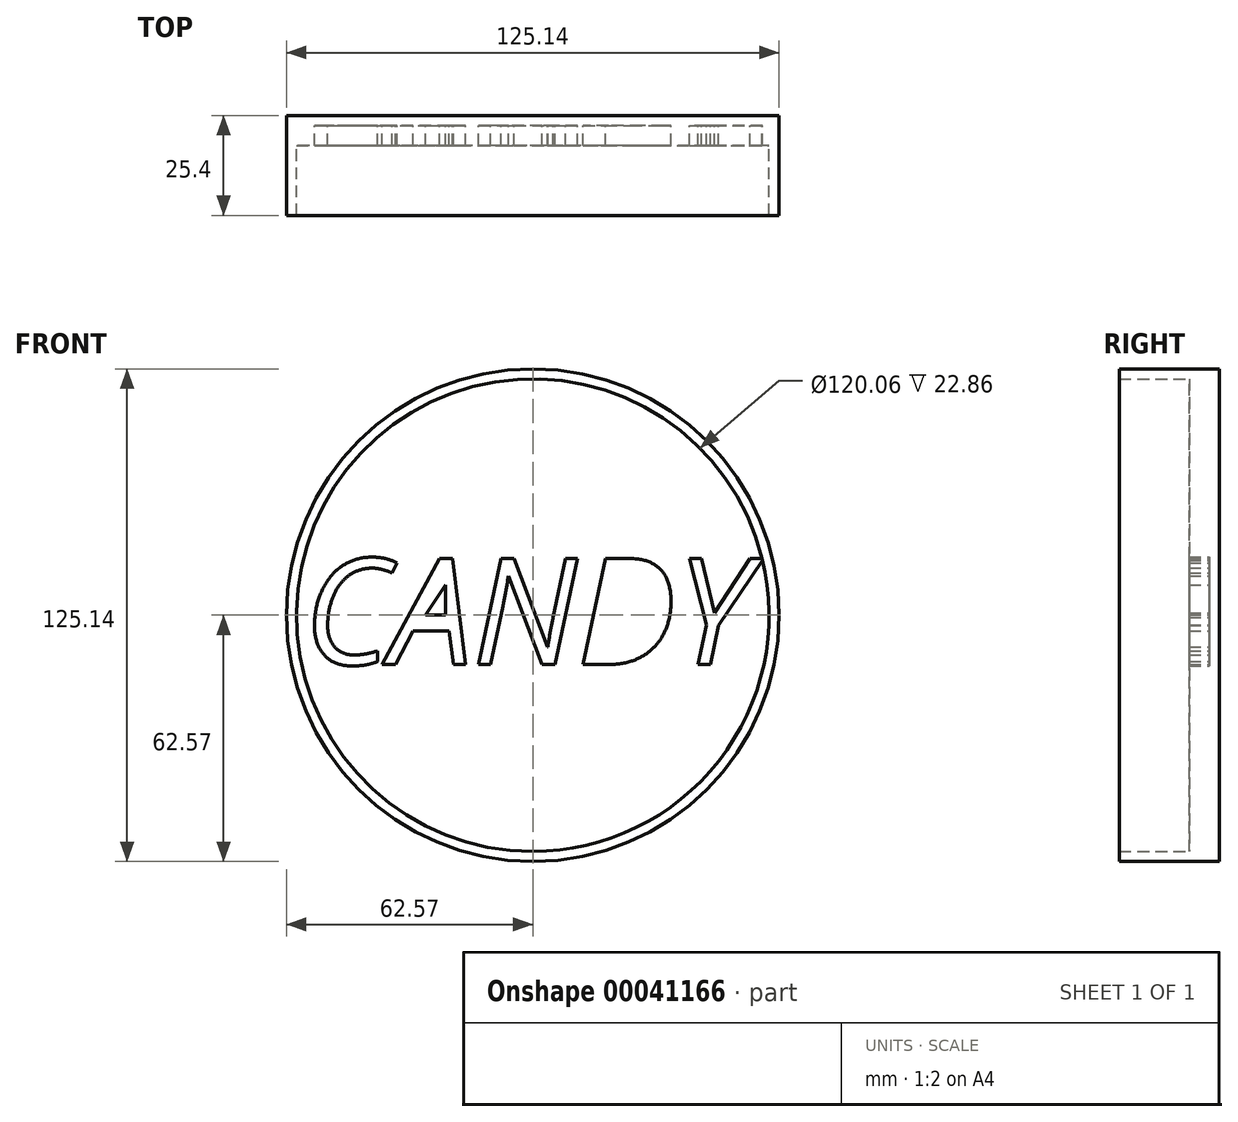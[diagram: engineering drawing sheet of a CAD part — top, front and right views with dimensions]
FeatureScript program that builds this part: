
annotation { "Feature Type Name" : "Feature", "Feature Type Description" : "" }
export const myFeature = defineFeature(function(context is Context, id is Id, definition is map)
    precondition{}
    {
        {
            var Q0;
            Q0=qCreatedBy(makeId("Front.planeOp"),FACE);
            var sketch = newSketch(context, id + "F0", { "sketchPlane" : qUnion([Q0])});
            skCircle(sketch, "E0", {"center": v(0, 0) * mm, "radius": 62.57 * mm});
            skSolve(sketch);
        }
        {
            var Q0;
            Q0=makeQuery(id+"F0.imprint","IMPRINT",FACE,{"disambiguationData":[TD([[makeQuery(id+"F0.imprint","IMPRINT",EDGE,{"derivedFrom":sQuery(id+"F0.wireOp",EDGE,"E0")}),1.0]])]});
            extrude(context, id + "F1", {"entities" : qUnion([Q0]), "depth" : 25.4 * mm});
        }
        {
            var Q0;
            Q0=makeQuery(id+"F1.opExtrude","CAP_FACE",FACE,{"disambiguationData":[OSD([sQuery(id+"F0.wireOp",EDGE,"E0")])],"isStart":false});
            shell(context, id + "F2", {"entities" : qUnion([Q0]), "thickness" : 2.54 * mm});
        }
        {
            var Q0;
            {var subQ0=sQuery(id+"F0.wireOp",EDGE,"E0");Q0=makeQuery(id+"F2.opShell","OFFSET_FACE",FACE,{"disambiguationData":[OSD([subQ0]),TDD([makeQuery(id+"F1.opExtrude","CAP_FACE",FACE,{"disambiguationData":[OSD([subQ0])],"isStart":true})])]});}
            var sketch = newSketch(context, id + "F3", { "sketchPlane" : qUnion([Q0])});
            skText(sketch, "E1", { "text": "CANDY", "fontName": "OpenSans-Italic.ttf"});
            const initialGuessF3  = {"E1": [-0.05823, -0.01253, 1, 0, 0.02713]};
            skSetInitialGuess(sketch, initialGuessF3);
            skSolve(sketch);
        }
        {
            var Q0;
            Q0=makeQuery(id+"F3.imprint","IMPRINT",FACE,{"disambiguationData":[TD([[makeQuery(id+"F3.imprint","IMPRINT",EDGE,{"derivedFrom":sQuery(id+"F3.wireOp",EDGE,"E1.sketch_text.stroke-0")}),1.0]])]});
            extrude(context, id + "F4", {"entities" : qUnion([Q0]), "operationType" : NewBodyOperationType.ADD, "depth" : 5.08 * mm});
        }
        {
            var Q0;
            {var subQ0=sQuery(id+"F0.wireOp",EDGE,"E0");Q0=makeQuery(id+"F4.boolean.opBoolean","SPLIT",FACE,{"disambiguationData":[TD([makeQuery(id+"F4.opExtrude","SWEPT_FACE",FACE,{"disambiguationData":[OSD([sQuery(id+"F3.wireOp",EDGE,"E1.sketch_text.stroke-17")])]})])],"derivedFrom":makeQuery(id+"F2.opShell","OFFSET_FACE",FACE,{"disambiguationData":[OSD([subQ0]),TDD([makeQuery(id+"F1.opExtrude","CAP_FACE",FACE,{"disambiguationData":[OSD([subQ0])],"isStart":true})])]})});}
            var sketch = newSketch(context, id + "F5", { "sketchPlane" : qUnion([Q0])});
            skLineSegment(sketch, "E2", {"start": v(-27.18, 0) * mm, "end": v(-22.14, 0) * mm});
            skLineSegment(sketch, "E3", {"start": v(-22.14, 0) * mm, "end": v(-22.14, 7.7) * mm});
            skLineSegment(sketch, "E4", {"start": v(-22.14, 7.7) * mm, "end": v(-27.18, 0) * mm});
            skSolve(sketch);
        }
        {
            var Q0;
            Q0=makeQuery(id+"F5.imprint","IMPRINT",FACE,{"disambiguationData":[TD([[makeQuery(id+"F5.imprint","IMPRINT",EDGE,{"derivedFrom":sQuery(id+"F5.wireOp",EDGE,"E2")}),1.0]])]});
            extrude(context, id + "F6", {"entities" : qUnion([Q0]), "operationType" : NewBodyOperationType.ADD, "depth" : 5.08 * mm});
        }
    });
